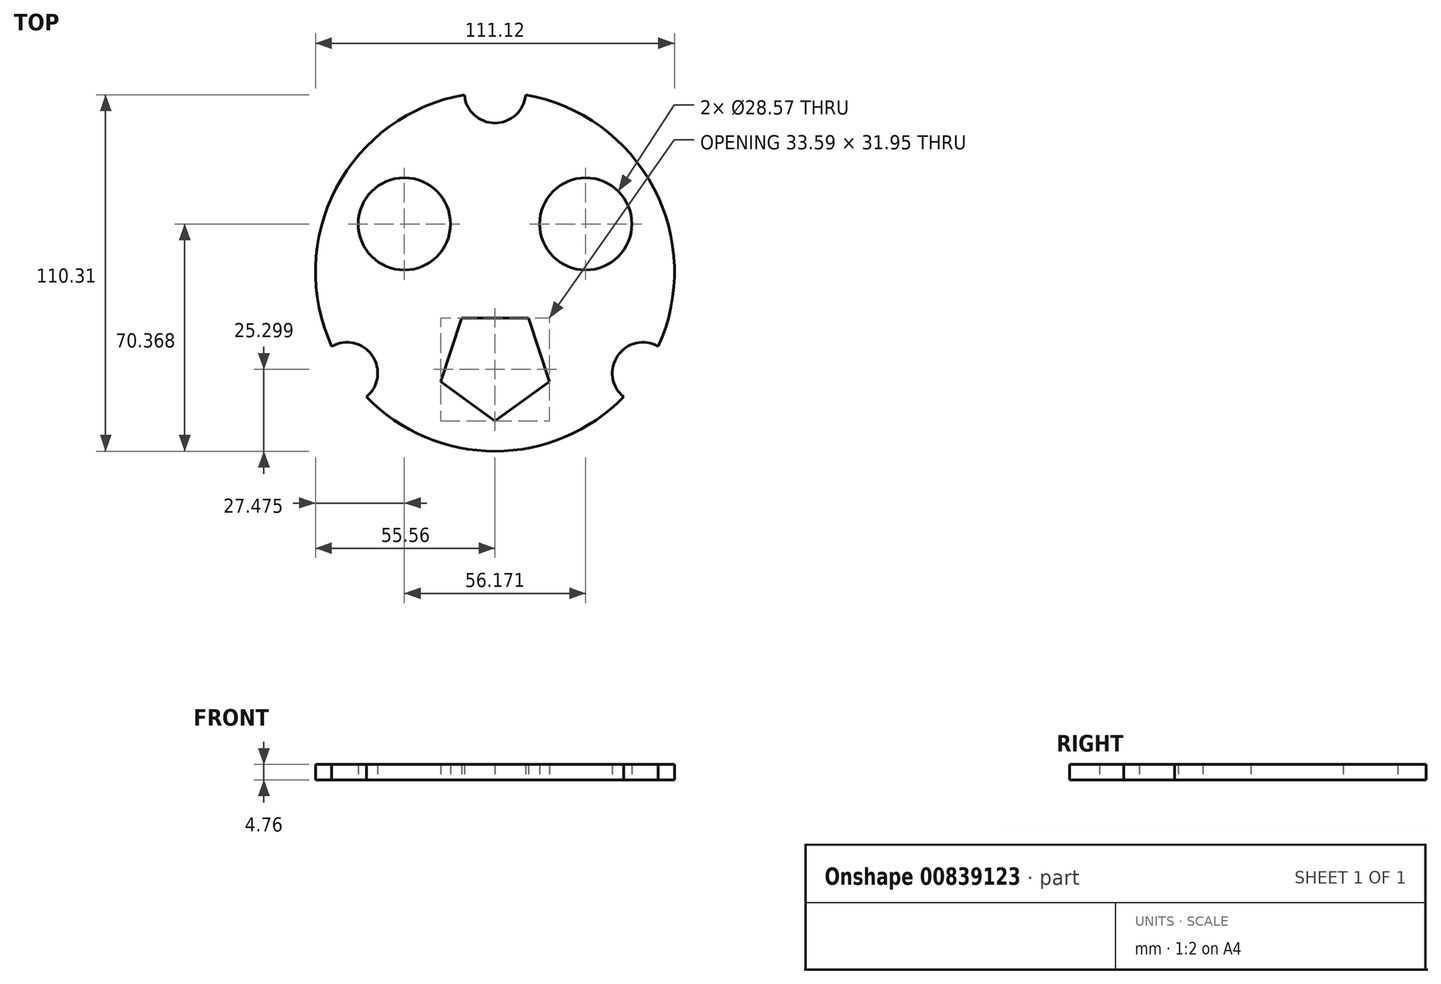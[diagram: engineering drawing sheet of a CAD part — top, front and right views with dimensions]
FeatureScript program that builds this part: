
annotation { "Feature Type Name" : "Feature", "Feature Type Description" : "" }
export const myFeature = defineFeature(function(context is Context, id is Id, definition is map)
    precondition{}
    {
        {
            var Q0;
            Q0=qCreatedBy(makeId("Top.planeOp"),FACE);
            var sketch = newSketch(context, id + "F0", { "sketchPlane" : qUnion([Q0])});
            skCircle(sketch, "E0", {"center": v(0, 0) * mm, "radius": 55.56 * mm});
            skSolve(sketch);
        }
        {
            var Q0;
            Q0=qCreatedBy(makeId("Top.planeOp"),FACE);
            var sketch = newSketch(context, id + "F1", { "sketchPlane" : qUnion([Q0])});
            skLineSegment(sketch, "E1", {"start": v(0, 0) * mm, "end": v(45.85, -31.4) * mm, "construction": true});
            skLineSegment(sketch, "E2", {"start": v(0, 0) * mm, "end": v(-45.85, -31.4) * mm, "construction": true});
            skLineSegment(sketch, "E3", {"start": v(0, 0) * mm, "end": v(0, 55.56) * mm, "construction": true});
            skCircle(sketch, "E4", {"center": v(0, 55.56) * mm, "radius": 9.53 * mm});
            skCircle(sketch, "E5", {"center": v(45.85, -31.4) * mm, "radius": 9.53 * mm});
            skCircle(sketch, "E6", {"center": v(-45.85, -31.4) * mm, "radius": 9.53 * mm});
            skLineSegment(sketch, "E7", {"start": v(0, 65.23) * mm, "end": v(0, -65.77) * mm, "construction": true});
            skCircle(sketch, "E8", {"center": v(0, 0) * mm, "radius": 55.56 * mm, "construction": true});
            skLineSegment(sketch, "E9", {"start": v(68.55, 0) * mm, "end": v(-87.1, 0) * mm, "construction": true});
            skSolve(sketch);
        }
        {
            var Q0;
            Q0 = qSketchRegion(id + "F0", true);
            extrude(context, id + "F2", {"entities" : qUnion([Q0]), "depth" : 4.76 * mm, "offsetDistance" : 25.4 * mm});
        }
        {
            var Q0;
            Q0=makeQuery(id+"F1.imprint","IMPRINT",FACE,{"disambiguationData":[TD([[makeQuery(id+"F1.imprint","IMPRINT",EDGE,{"derivedFrom":sQuery(id+"F1.wireOp",EDGE,"E6")}),1.0]])]});
            var Q1;
            Q1=makeQuery(id+"F1.imprint","IMPRINT",FACE,{"disambiguationData":[TD([[makeQuery(id+"F1.imprint","IMPRINT",EDGE,{"derivedFrom":sQuery(id+"F1.wireOp",EDGE,"E4")}),1.0]])]});
            var Q2;
            Q2=makeQuery(id+"F1.imprint","IMPRINT",FACE,{"disambiguationData":[TD([[makeQuery(id+"F1.imprint","IMPRINT",EDGE,{"derivedFrom":sQuery(id+"F1.wireOp",EDGE,"E5")}),1.0]])]});
            var Q3;
            Q3=makeQuery(id+"F2.opExtrude","CAP_FACE",FACE,{"disambiguationData":[OSD([sQuery(id+"F0.wireOp",EDGE,"E0"),sQuery(id+"F0.wireOp",EDGE,"bjsPy7cM-LU8B-mQyM-yG8y-nqjZCKy3CBnq")])],"isStart":false});
            extrude(context, id + "F3", {"entities" : qUnion([Q0, Q1, Q2]), "operationType" : NewBodyOperationType.REMOVE, "endBound" : BoundingType.UP_TO_SURFACE, "depth" : 25.4 * mm, "endBoundEntityFace" : qUnion([Q3]), "offsetDistance" : 25.4 * mm});
        }
        {
            var Q0;
            Q0=qCreatedBy(makeId("Top.planeOp"),FACE);
            var sketch = newSketch(context, id + "F4", { "sketchPlane" : qUnion([Q0])});
            skCircle(sketch, "E10", {"center": v(0, 0) * mm, "radius": 38.1 * mm, "construction": true});
            skLineSegment(sketch, "E11", {"start": v(0, 0) * mm, "end": v(0, 46.32) * mm, "construction": true});
            skLineSegment(sketch, "E12", {"start": v(0, 0) * mm, "end": v(-40.93, -28.03) * mm, "construction": true});
            skLineSegment(sketch, "E13", {"start": v(0, 0) * mm, "end": v(50.05, -34.27) * mm, "construction": true});
            skCircle(sketch, "E14", {"center": v(-35.9, -24.57) * mm, "radius": 0.64 * mm});
            skCircle(sketch, "E15", {"center": v(35.9, -24.57) * mm, "radius": 0.64 * mm});
            skCircle(sketch, "E16", {"center": v(0, 43.5) * mm, "radius": 0.64 * mm});
            skSolve(sketch);
        }
        {
            var Q0;
            Q0=makeQuery(id+"F2.opExtrude","CAP_FACE",FACE,{"disambiguationData":[OSD([sQuery(id+"F0.wireOp",EDGE,"E0"),sQuery(id+"F0.wireOp",EDGE,"bjsPy7cM-LU8B-mQyM-yG8y-nqjZCKy3CBnq")])],"isStart":true});
            var sketch = newSketch(context, id + "F5", { "sketchPlane" : qUnion([Q0])});
            skLineSegment(sketch, "E17", {"start": v(0, 0) * mm, "end": v(0, 55.56) * mm, "construction": true});
            skLineSegment(sketch, "E18", {"start": v(0, 0) * mm, "end": v(68.02, -35.86) * mm, "construction": true});
            skLineSegment(sketch, "E19", {"start": v(0, 0) * mm, "end": v(-62.35, -32.87) * mm, "construction": true});
            skCircle(sketch, "E20.cCircle", {"center": v(0, 28.58) * mm, "radius": 14.29 * mm, "construction": true});
            skLineSegment(sketch, "E20.0", {"start": v(0, 46.24) * mm, "end": v(16.8, 34.03) * mm});
            skLineSegment(sketch, "E20.1", {"start": v(16.8, 34.03) * mm, "end": v(10.38, 14.29) * mm});
            skLineSegment(sketch, "E20.2", {"start": v(10.38, 14.29) * mm, "end": v(-10.38, 14.29) * mm});
            skLineSegment(sketch, "E20.3", {"start": v(-10.38, 14.29) * mm, "end": v(-16.8, 34.03) * mm});
            skLineSegment(sketch, "E20.4", {"start": v(-16.8, 34.03) * mm, "end": v(0, 46.24) * mm});
            skPoint(sketch, "E20.0.midPoint", {"position": v(8.4, 40.13) * mm});
            skCircle(sketch, "E21", {"center": v(-28.09, -14.8) * mm, "radius": 14.29 * mm});
            skCircle(sketch, "E22", {"center": v(28.09, -14.8) * mm, "radius": 14.29 * mm});
            skSolve(sketch);
        }
        {
            var Q0;
            Q0=makeQuery(id+"F5.imprint","IMPRINT",FACE,{"disambiguationData":[TD([[makeQuery(id+"F5.imprint","IMPRINT",EDGE,{"derivedFrom":sQuery(id+"F5.wireOp",EDGE,"E21")}),1.0]])]});
            var Q1;
            Q1=makeQuery(id+"F5.imprint","IMPRINT",FACE,{"disambiguationData":[TD([[makeQuery(id+"F5.imprint","IMPRINT",EDGE,{"derivedFrom":sQuery(id+"F5.wireOp",EDGE,"E22")}),1.0]])]});
            var Q2;
            Q2=makeQuery(id+"F5.imprint","IMPRINT",FACE,{"disambiguationData":[TD([[makeQuery(id+"F5.imprint","IMPRINT",EDGE,{"derivedFrom":sQuery(id+"F5.wireOp",EDGE,"E20.0")}),-1.0]])]});
            extrude(context, id + "F6", {"entities" : qUnion([Q0, Q1, Q2]), "operationType" : NewBodyOperationType.REMOVE, "oppositeDirection" : true, "depth" : 25.4 * mm, "offsetDistance" : 25.4 * mm});
        }
    });
